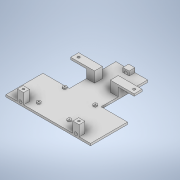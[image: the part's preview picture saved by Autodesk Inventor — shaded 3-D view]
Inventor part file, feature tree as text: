
AUTODESK INVENTOR PART (.ipt)
format: ipt  version: 2020 (Build 240168000, 168)  size: 261,120 bytes
history: native  units: mm
features: sketch x10, extrude x6, hole x5, mirror x1
ambient origin geometry x8: Origin, YZ Plane, XZ Plane, XY Plane, X Axis, Y Axis, Z Axis, Center Point
bodies: Solid1 (feature_tree)
feature tree (22):
  extrude  "Extrusion1"  Depth=30.0mm
  sketch  "Sketch2"  dims[d2=50.0mm d3=70.0mm]
  extrude  "Extrusion2"  Depth=70.0mm
  extrude  "Extrusion4"  Depth=12.0mm
  extrude  "Extrusion5"  Depth=6.0mm
  extrude  "Extrusion6"  Depth=6.0mm
  hole  "Hole5"  [1 undecoded]
  mirror  "Mirror1"
  extrude  "Extrusion3"  Depth=8.0mm
  hole  "Hole3"  [1 undecoded]
  hole  "Hole2"  [1 undecoded]
  hole  "Hole1"  [1 undecoded]
  hole  "Hole4"  [1 undecoded]
  sketch  "Sketch1"  dims[d0=158.0mm d1=30.0mm]
  sketch  "Sketch3"  dims[d4=4.0mm d5=0.0mm d6=12.0mm]
  sketch  "Sketch4"  dims[d7=11.0mm d8=6.0mm]
  sketch  "Sketch5"  dims[d9=8.0mm d10=0.0mm d11=6.0mm]
  sketch  "Sketch6"  dims[d12=6.0mm]
  sketch  "Sketch7"  dims[d13=5.9mm d14=6.0mm d15=4.0mm d16=2.0mm d17=90.0deg d18=8.0mm d19=0.0mm d21=6.0mm]
  sketch  "Sketch9"  dims[d22=6.0mm]
  sketch  "Sketch10"  dims[d24=5.9mm d25=6.0mm d26=4.0mm d27=2.0mm d28=90.0deg d29=8.0mm d30=0.0mm d31=58.0mm]
  sketch  "Sketch11"  dims[d32=49.0mm d33=7.0mm d34=2.0mm d35=0.0mm d36=1.8mm d37=6.0mm d38=4.0mm d39=2.0mm d40=90.0deg d41=8.0mm d42=0.0mm d45=42.0mm d50=20.0mm d51=0.0mm d52=46.5mm d53=6.0mm d54=6.0mm d55=4.1mm d56=6.0mm d57=4.0mm d58=2.0mm d59=90.0deg d60=6.0mm d61=0.0mm d63=110.0mm d64=15.0mm d65=15.0mm d66=20.0mm d67=0.0mm d68=4.0mm d69=30.0mm d70=0.0mm d71=7.5mm d72=4.6mm d73=6.0mm d74=4.0mm d75=2.0mm d76=90.0deg d77=6.0mm d78=0.0mm d79=13.0mm]
note: 5 required parameter values undecoded (feature->parameter linkage not recoverable at this tier; creation-order binding heuristic only, values carry confidence <= 0.55)
